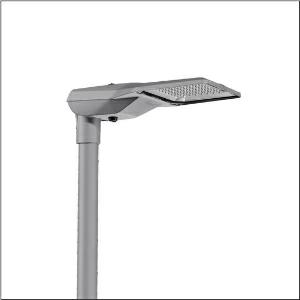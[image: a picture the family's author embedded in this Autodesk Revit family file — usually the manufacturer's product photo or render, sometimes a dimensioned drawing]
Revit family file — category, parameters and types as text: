
# Revit family: streetlight_sl_21_iq_midi___st0_5a_5xe3b31y08mb_2f18
name_source: partatom
category: Lighting Fixtures
units: mm (PartAtom-declared; Revit-internal decimal feet)

## family parameters
Cut with Voids When Loaded = No
Host = Face
Light Source = No
Part Type = Normal
Room Calculation Point = No
Round Connector Dimension = Use Diameter
Shared = No

## types (1)
- --- (1 x LED, 18340 lm, 129.3 W, 3000K)
    Apparent Load = 129 VA
    CIE Flux Codes = 41 75 97 100 100
    Color Rendering = 70
    Color Temperature = 3000K
    Default Elevation = 1800 mm
    Description = Streetlight SL 21 iQ midi, mast luminaire, primary light control with lens, of PMMA, primary optical cover: cover, of toughened safety glass, transparent, light distribution: ST0.5a, light emission: direct distribution, primary light characteristic: asymmetric, installation type: post-top, side-entry, LED, High Power LED, rated luminous flux: 18.340lm, luminous efficacy: 142lm/W, light colour: 730, colour temperature: 3000K, control: presetting dimming logarithmic, Street-Remote, Auto-Match, Temp-Guard, Lumen-Switch, Night-Set, Smart-Wire, Light-Fading, Desk-Remote (wireless, voltage-free reading and setting of iQ features in the workshop via application-optimized NFC function/RFID function), optimised constant luminous flux control (CLO 2.0), mains connection: 230..240V, AC, 50/60Hz, start of lifetime: 129W, end of service life: 142W, reduction: 56W, luminaire housing, of diecast aluminium, powder-coated, Siteco® metallic grey (DB 702S), corrosivity category C5 mid according to DIN EN ISO 12944, please order mast flange separately, inclination adjustable: 0°, 5°, 10°, 15°, sealing non-destructively replaceable, multi-level sealing system, length: 644mm, width: 335mm, height: 110mm, mast flange for spigot size: 42mm (side-entry): 5XC10008XM4, 60/48mm (side-entry/post-top): 5XC10108XM2, 76/60mm (side-entry/post-top): 5XC10108XM1, Smart Interface below and above, protection rating (complete): IP66, insulation class (complete): insulation class II (safety insulation), certification: CE, ENEC, ENEC+, VDE, impact resistance: IK09, permissible operating ambient temperature for outdoor applications: -40..+50°C, standard-compliant lighting for roads and squares, packaging unit: 1 piece

Light Distribution: ST0.5a
    Height = 111 mm
    Lamp = 1 x LED
    Lamp Light Flux = 18340 lm
    Lamp Power = 129.3 W
    Lamp count = 1
    Length = 644 mm
    Luminous efficacy = 142 lm/W
    Manufacturer = Siteco
    ModVariant = No
    Model = 5XE3B31Y08MB
    Number of Poles = 1
    OnlyDefault = Yes
    Power Factor = 1
    Product Name = Streetlight SL 21 iQ midi | ST0.5a
    Product group = mast luminaire | pylon top
    ProductGroupID = 6100
    Protection Class = Protection class II
    Protection Degree = IP 66
    RLX_Detail_Level = 1
    RLX_Emergency_Light_Flux = 0 lm
    RLX_Emergency_Type = 0
    RLX_Emergency_Type_DB = No
    RlxData = <blob elided: 101777 chars, md5=bbc8cda6>
    Socket = socket
    Standby Power = 0 W
    System Light Flux = 18340 lm
    System Power = 129 W
    Type Comments = factory setting: luminous flux: 100 % | dim-lin: 254 | 672 mA
    Type Image = l_1004304.jpg
    URL = http://relux.com
    VarID = @adj_064263
    Voltage = 0 V
    Weight = 0.00 kg
    Width = 336 mm

## geometry (parser evidence)
native form markers: Blend x4, Sweep x11
no freeform markers — native parametric forms only
